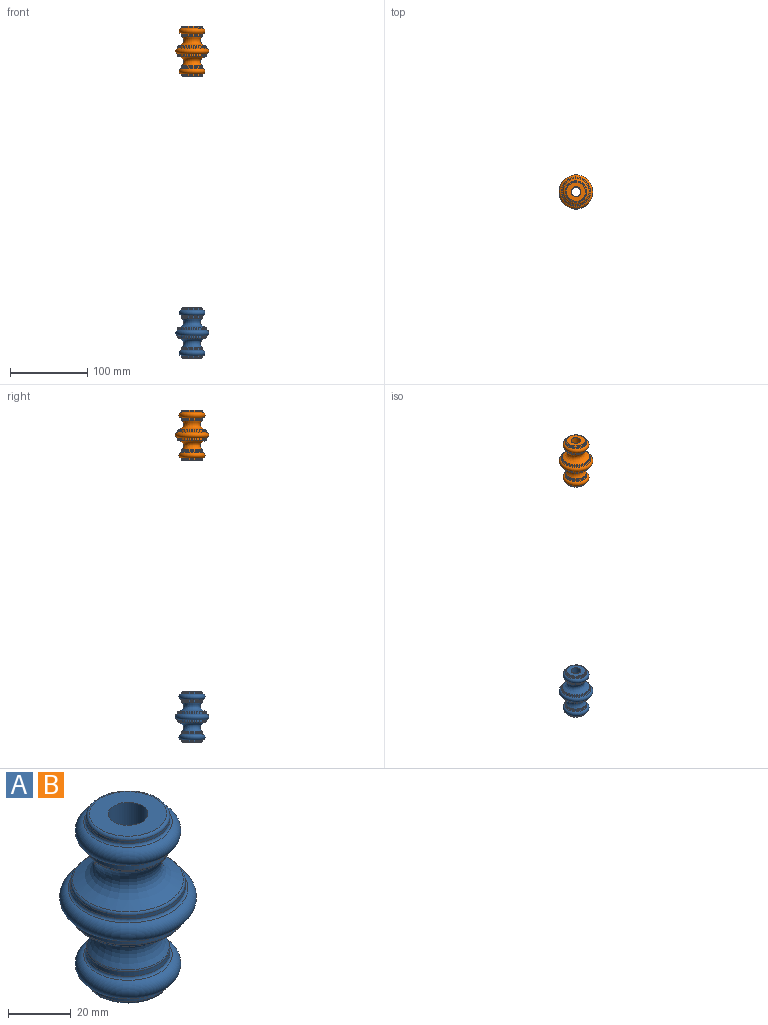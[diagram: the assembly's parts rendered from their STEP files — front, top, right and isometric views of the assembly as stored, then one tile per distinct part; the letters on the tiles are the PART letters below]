
ASSEMBLY  parts=2 mates=2
PART A: 26 faces, bbox 47.3x47.3x65 mm
  f0: cylinder r=18.35mm len=36.7mm, axis (0,0,1), area 161.5mm2, adj f1,f25
  f1: torus R=17.35mm, axis (0,0,1), area 139.4mm2, adj f0,f2
  f2: revolved ~35.38x35.38mm, area 1336.9mm2, adj f1,f3
  f3: torus R=12.35mm, axis (0,0,1), area 53.9mm2, adj f2,f4
  f4: cylinder r=13.35mm len=26.7mm, axis (0,0,1), area 148.8mm2, adj f3,f5
  f5: torus R=14.35mm, axis (0,0,1), area 115.3mm2, adj f4,f6
  f6: torus R=13.35mm, axis (0,0,1), area 940.8mm2, adj f5,f7
  f7: torus R=14.35mm, axis (0,0,1), area 115.3mm2, adj f6,f8
  f8: cylinder r=13.35mm len=26.7mm, axis (0,0,1), area 93.3mm2, adj f7,f9
  f9: torus R=12.35mm, axis (0,0,1), area 128.2mm2, adj f8,f10
  f10: plane 24.7x24.7mm, normal (0,0,1), area 352.5mm2, adj f9,f11
  f11: cylinder r=6.35mm len=65mm, axis (0,0,1), area 2593.4mm2, adj f10,f12
  f12: plane 24.7x24.7mm, normal (0,0,-1), area 352.5mm2, adj f11,f13
  f13: torus R=12.35mm, axis (0,0,1), area 128.2mm2, adj f12,f14
  f14: cylinder r=13.35mm len=26.7mm, axis (0,0,1), area 93.3mm2, adj f13,f15
  f15: torus R=14.35mm, axis (0,0,1), area 115.3mm2, adj f14,f16
  f16: torus R=13.35mm, axis (0,0,1), area 940.8mm2, adj f15,f17
  f17: torus R=14.35mm, axis (0,0,1), area 115.3mm2, adj f16,f18
  f18: cylinder r=13.35mm len=26.7mm, axis (0,0,1), area 148.8mm2, adj f17,f19
  f19: torus R=12.35mm, axis (0,0,1), area 53.9mm2, adj f18,f20
  f20: revolved ~35.38x35.38mm, area 1336.9mm2, adj f19,f21
  f21: torus R=17.35mm, axis (0,0,1), area 139.4mm2, adj f20,f22
  f22: cylinder r=18.35mm len=36.7mm, axis (0,0,1), area 161.5mm2, adj f21,f23
  f23: torus R=19.35mm, axis (0,0,1), area 157.6mm2, adj f22,f24
  f24: torus R=18.35mm, axis (0,0,1), area 1237mm2, adj f23,f25
  f25: torus R=19.35mm, axis (0,0,1), area 157.6mm2, adj f0,f24
PART B: same geometry as A
PLACE A t=(-93.84,190.12,142.43)mm
PLACE B t=(-93.84,190.12,507.43)mm
MATE planar B.f0 <-> A.f0  axis (0,0,1) through (-93.84,190.12,539.93)mm
MATE cylindrical A.f0 <-> B.f0  axis (0,0,1) through (-93.84,190.12,174.93)mm
